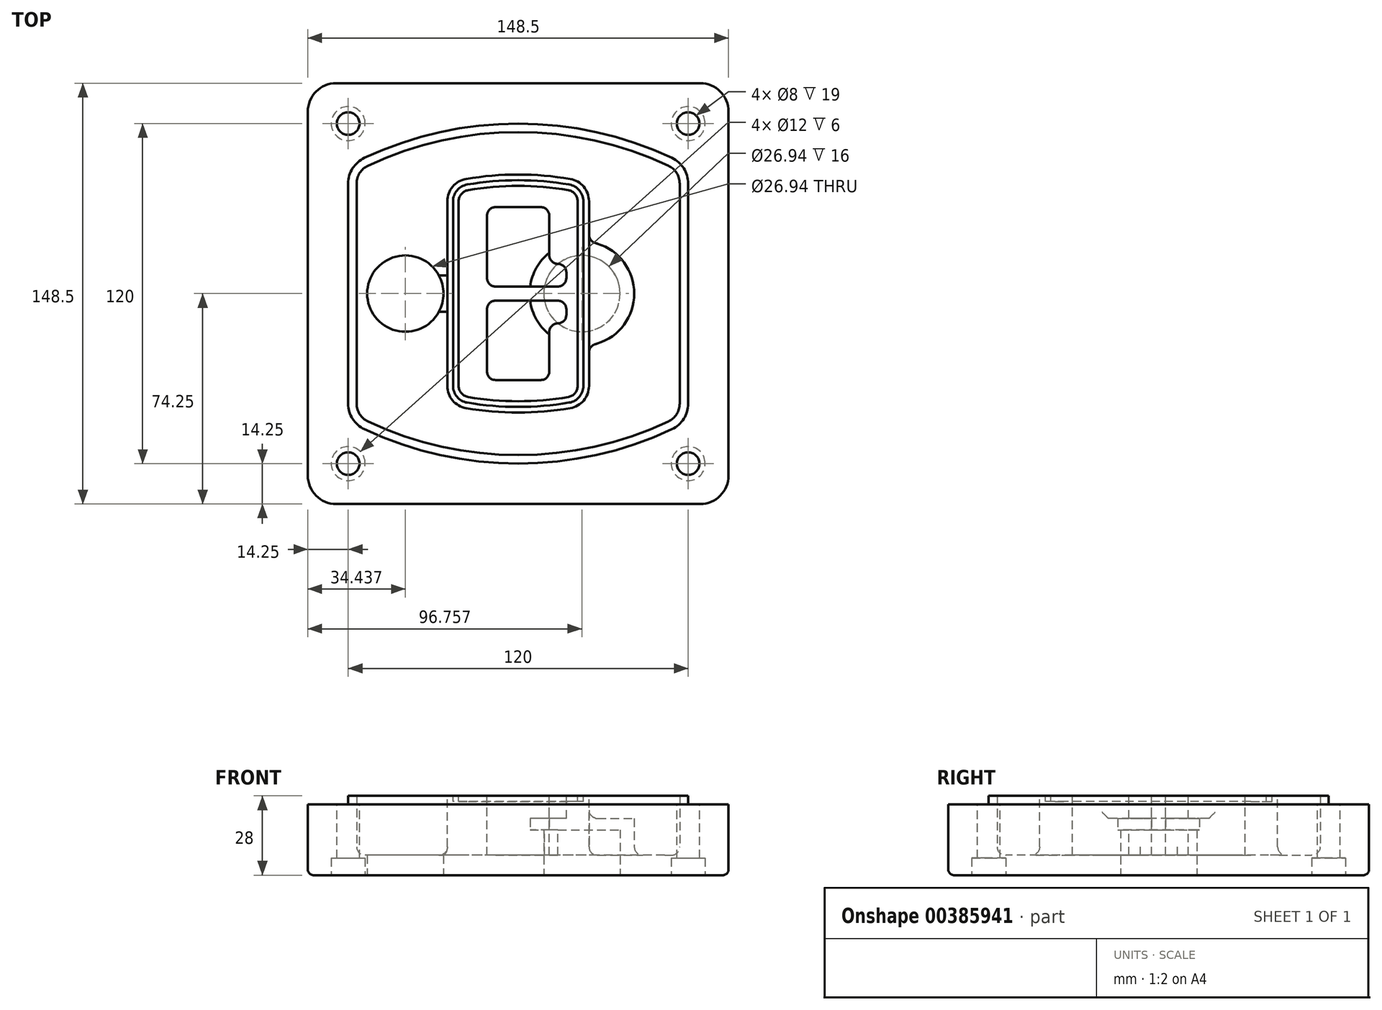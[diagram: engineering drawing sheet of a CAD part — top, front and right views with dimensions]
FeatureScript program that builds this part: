
annotation { "Feature Type Name" : "Feature", "Feature Type Description" : "" }
export const myFeature = defineFeature(function(context is Context, id is Id, definition is map)
    precondition{}
    {
        {
            var Q0;
            Q0=qCreatedBy(makeId("Top.planeOp"),FACE);
            var sketch = newSketch(context, id + "F0", { "sketchPlane" : qUnion([Q0])});
            skPoint(sketch, "E0.rect.middle", {"position": v(0, 0) * mm});
            skLineSegment(sketch, "E1.bottom", {"start": v(-64.25, -74.25) * mm, "end": v(64.25, -74.25) * mm});
            skLineSegment(sketch, "E1.top", {"start": v(-64.25, 74.25) * mm, "end": v(64.25, 74.25) * mm});
            skLineSegment(sketch, "E1.left", {"start": v(-74.25, -64.25) * mm, "end": v(-74.25, 64.25) * mm});
            skLineSegment(sketch, "E1.right", {"start": v(74.25, -64.25) * mm, "end": v(74.25, 64.25) * mm});
            skLineSegment(sketch, "E2", {"start": v(-74.25, 74.25) * mm, "end": v(74.25, -74.25) * mm, "construction": true});
            skLineSegment(sketch, "E3", {"start": v(74.25, 74.25) * mm, "end": v(-74.25, -74.25) * mm, "construction": true});
            skCircle(sketch, "E4", {"center": v(-60, 60) * mm, "radius": 4 * mm});
            skCircle(sketch, "E5", {"center": v(60, 60) * mm, "radius": 4 * mm});
            skCircle(sketch, "E6", {"center": v(60, -60) * mm, "radius": 4 * mm});
            skCircle(sketch, "E7", {"center": v(-60, -60) * mm, "radius": 4 * mm});
            skLineSegment(sketch, "E8", {"start": v(-60, 60) * mm, "end": v(60, 60) * mm, "construction": true});
            skLineSegment(sketch, "E9", {"start": v(60, 60) * mm, "end": v(60, -60) * mm, "construction": true});
            skLineSegment(sketch, "E10", {"start": v(60, -60) * mm, "end": v(-60, -60) * mm, "construction": true});
            skLineSegment(sketch, "E11", {"start": v(-60, -60) * mm, "end": v(-60, 60) * mm, "construction": true});
            skLineSegment(sketch, "E12", {"start": v(-60, 38.83) * mm, "end": v(-60, -38.83) * mm});
            skLineSegment(sketch, "E13", {"start": v(60, 38.83) * mm, "end": v(60, -38.83) * mm});
            skArc(sketch, "E14", {"start": v(54.26, 47.88) * mm, "mid": v(0, 60) * mm, "end": v(-54.26, 47.88) * mm});
            skArc(sketch, "E15", {"start": v(-54.26, -47.88) * mm, "mid": v(0, -60) * mm, "end": v(54.26, -47.88) * mm});
            skLineSegment(sketch, "E16", {"start": v(-60, 0) * mm, "end": v(60, 0) * mm, "construction": true});
            skPoint(sketch, "E17.visualSharp", {"position": v(-60, -45) * mm});
            skArc(sketch, "E17.filletArc", {"start": v(-60, -38.83) * mm, "mid": v(-58.44, -44.2) * mm, "end": v(-54.26, -47.88) * mm});
            skPoint(sketch, "E18.visualSharp", {"position": v(-60, 45) * mm});
            skArc(sketch, "E18.filletArc", {"start": v(-54.26, 47.88) * mm, "mid": v(-58.44, 44.2) * mm, "end": v(-60, 38.83) * mm});
            skPoint(sketch, "E19.visualSharp", {"position": v(60, 45) * mm});
            skArc(sketch, "E19.filletArc", {"start": v(60, 38.83) * mm, "mid": v(58.44, 44.2) * mm, "end": v(54.26, 47.88) * mm});
            skPoint(sketch, "E20.visualSharp", {"position": v(60, -45) * mm});
            skArc(sketch, "E20.filletArc", {"start": v(54.26, -47.88) * mm, "mid": v(58.44, -44.2) * mm, "end": v(60, -38.83) * mm});
            skPoint(sketch, "E21.visualSharp", {"position": v(-74.25, 74.25) * mm});
            skArc(sketch, "E21.filletArc", {"start": v(-64.25, 74.25) * mm, "mid": v(-71.32, 71.32) * mm, "end": v(-74.25, 64.25) * mm});
            skPoint(sketch, "E22.visualSharp", {"position": v(74.25, 74.25) * mm});
            skArc(sketch, "E22.filletArc", {"start": v(74.25, 64.25) * mm, "mid": v(71.32, 71.32) * mm, "end": v(64.25, 74.25) * mm});
            skPoint(sketch, "E23.visualSharp", {"position": v(74.25, -74.25) * mm});
            skArc(sketch, "E23.filletArc", {"start": v(64.25, -74.25) * mm, "mid": v(71.32, -71.32) * mm, "end": v(74.25, -64.25) * mm});
            skPoint(sketch, "E24.visualSharp", {"position": v(-74.25, -74.25) * mm});
            skArc(sketch, "E24.filletArc", {"start": v(-74.25, -64.25) * mm, "mid": v(-71.32, -71.32) * mm, "end": v(-64.25, -74.25) * mm});
            skArc(sketch, "E25.0", {"start": v(57, 38.83) * mm, "mid": v(55.9, 42.58) * mm, "end": v(52.98, 45.17) * mm});
            skLineSegment(sketch, "E25.1", {"start": v(57, 38.83) * mm, "end": v(57, -38.83) * mm});
            skArc(sketch, "E25.2", {"start": v(52.98, -45.17) * mm, "mid": v(55.9, -42.58) * mm, "end": v(57, -38.83) * mm});
            skArc(sketch, "E25.3", {"start": v(-52.98, -45.17) * mm, "mid": v(0, -57) * mm, "end": v(52.98, -45.17) * mm});
            skArc(sketch, "E25.4", {"start": v(-57, -38.83) * mm, "mid": v(-55.9, -42.58) * mm, "end": v(-52.98, -45.17) * mm});
            skArc(sketch, "E25.5", {"start": v(52.98, 45.17) * mm, "mid": v(0, 57) * mm, "end": v(-52.98, 45.17) * mm});
            skLineSegment(sketch, "E25.6", {"start": v(-57, 38.83) * mm, "end": v(-57, -38.83) * mm});
            skArc(sketch, "E25.7", {"start": v(-52.98, 45.17) * mm, "mid": v(-55.9, 42.58) * mm, "end": v(-57, 38.83) * mm});
            skArc(sketch, "E26.0", {"start": v(-55.96, 51.5) * mm, "mid": v(-61.82, 46.33) * mm, "end": v(-64, 38.83) * mm});
            skArc(sketch, "E26.1", {"start": v(55.96, 51.5) * mm, "mid": v(0, 64) * mm, "end": v(-55.96, 51.5) * mm});
            skArc(sketch, "E26.2", {"start": v(64, 38.83) * mm, "mid": v(61.82, 46.33) * mm, "end": v(55.96, 51.5) * mm});
            skLineSegment(sketch, "E26.3", {"start": v(64, 38.83) * mm, "end": v(64, -38.83) * mm});
            skArc(sketch, "E26.4", {"start": v(55.96, -51.5) * mm, "mid": v(61.82, -46.33) * mm, "end": v(64, -38.83) * mm});
            skLineSegment(sketch, "E26.5", {"start": v(-64, 38.83) * mm, "end": v(-64, -38.83) * mm});
            skArc(sketch, "E26.6", {"start": v(-55.96, -51.5) * mm, "mid": v(0, -64) * mm, "end": v(55.96, -51.5) * mm});
            skArc(sketch, "E26.7", {"start": v(-64, -38.83) * mm, "mid": v(-61.82, -46.33) * mm, "end": v(-55.96, -51.5) * mm});
            skCircle(sketch, "E27", {"center": v(0, 95) * mm, "radius": 6 * mm});
            skArc(sketch, "E28", {"start": v(7.76, 95) * mm, "mid": v(-7.24, 110.1) * mm, "end": v(-22.24, 95) * mm});
            skSolve(sketch);
        }
        {
            var Q0;
            Q0=makeQuery(id+"F0.imprint","IMPRINT",FACE,{"disambiguationData":[TD([[makeQuery(id+"F0.imprint","IMPRINT",EDGE,{"derivedFrom":sQuery(id+"F0.wireOp",EDGE,"E1.bottom")}),1.0]])]});
            var Q1;
            Q1=makeQuery(id+"F0.imprint","IMPRINT",FACE,{"disambiguationData":[TD([[makeQuery(id+"F0.imprint","IMPRINT",EDGE,{"derivedFrom":sQuery(id+"F0.wireOp",EDGE,"E12")}),1.0]])]});
            var Q2;
            Q2=makeQuery(id+"F0.imprint","IMPRINT",FACE,{"disambiguationData":[TD([[makeQuery(id+"F0.imprint","IMPRINT",EDGE,{"derivedFrom":sQuery(id+"F0.wireOp",EDGE,"E25.0")}),1.0]])]});
            var Q3;
            Q3=makeQuery(id+"F0.imprint","IMPRINT",FACE,{"disambiguationData":[TD([[makeQuery(id+"F0.imprint","IMPRINT",EDGE,{"derivedFrom":sQuery(id+"F0.wireOp",EDGE,"E12")}),-1.0]])]});
            extrude(context, id + "F1", {"entities" : qUnion([Q0, Q1, Q2, Q3]), "oppositeDirection" : true, "depth" : 25 * mm});
        }
        {
            var Q0;
            Q0=makeQuery(id+"F0.imprint","IMPRINT",FACE,{"disambiguationData":[TD([[makeQuery(id+"F0.imprint","IMPRINT",EDGE,{"derivedFrom":sQuery(id+"F0.wireOp",EDGE,"E12")}),1.0]])]});
            extrude(context, id + "F2", {"entities" : qUnion([Q0]), "operationType" : NewBodyOperationType.ADD, "depth" : 3 * mm});
        }
        {
            var Q0;
            Q0=makeQuery(id+"F0.imprint","IMPRINT",FACE,{"disambiguationData":[TD([[makeQuery(id+"F0.imprint","IMPRINT",EDGE,{"derivedFrom":sQuery(id+"F0.wireOp",EDGE,"E25.0")}),1.0]])]});
            extrude(context, id + "F3", {"entities" : qUnion([Q0]), "operationType" : NewBodyOperationType.REMOVE, "oppositeDirection" : true, "depth" : 18 * mm});
        }
        {
            var Q0;
            Q0=makeQuery(id+"F2.opExtrude","CAP_FACE",FACE,{"disambiguationData":[OSD([sQuery(id+"F0.wireOp",EDGE,"E12"),sQuery(id+"F0.wireOp",EDGE,"E13"),sQuery(id+"F0.wireOp",EDGE,"E14"),sQuery(id+"F0.wireOp",EDGE,"E15"),sQuery(id+"F0.wireOp",EDGE,"E17.filletArc"),sQuery(id+"F0.wireOp",EDGE,"E18.filletArc"),sQuery(id+"F0.wireOp",EDGE,"E19.filletArc"),sQuery(id+"F0.wireOp",EDGE,"E20.filletArc"),sQuery(id+"F0.wireOp",EDGE,"E25.0"),sQuery(id+"F0.wireOp",EDGE,"E25.1"),sQuery(id+"F0.wireOp",EDGE,"E25.2"),sQuery(id+"F0.wireOp",EDGE,"E25.3"),sQuery(id+"F0.wireOp",EDGE,"E25.4"),sQuery(id+"F0.wireOp",EDGE,"E25.5"),sQuery(id+"F0.wireOp",EDGE,"E25.6"),sQuery(id+"F0.wireOp",EDGE,"E25.7")])],"isStart":false});
            var sketch = newSketch(context, id + "F4", { "sketchPlane" : qUnion([Q0])});
            skArc(sketch, "E29.0", {"start": v(-18.34, -40.45) * mm, "mid": v(0, -42) * mm, "end": v(18.34, -40.45) * mm});
            skArc(sketch, "E30.0", {"start": v(18.34, 40.45) * mm, "mid": v(0, 42) * mm, "end": v(-18.34, 40.45) * mm});
            skLineSegment(sketch, "E31", {"start": v(-25, 32.57) * mm, "end": v(-25, -32.57) * mm});
            skLineSegment(sketch, "E32", {"start": v(25, 32.57) * mm, "end": v(25, -32.57) * mm});
            skLineSegment(sketch, "E33", {"start": v(-25, 39.1) * mm, "end": v(25, 39.1) * mm, "construction": true});
            skLineSegment(sketch, "E34", {"start": v(-25, -39.1) * mm, "end": v(25, -39.1) * mm, "construction": true});
            skPoint(sketch, "E35.visualSharp", {"position": v(-25, 39.1) * mm});
            skArc(sketch, "E35.filletArc", {"start": v(-18.34, 40.45) * mm, "mid": v(-23.11, 37.73) * mm, "end": v(-25, 32.57) * mm});
            skPoint(sketch, "E36.visualSharp", {"position": v(25, 39.1) * mm});
            skArc(sketch, "E36.filletArc", {"start": v(25, 32.57) * mm, "mid": v(23.11, 37.73) * mm, "end": v(18.34, 40.45) * mm});
            skPoint(sketch, "E37.visualSharp", {"position": v(25, -39.1) * mm});
            skArc(sketch, "E37.filletArc", {"start": v(18.34, -40.45) * mm, "mid": v(23.11, -37.73) * mm, "end": v(25, -32.57) * mm});
            skPoint(sketch, "E38.visualSharp", {"position": v(-25, -39.1) * mm});
            skArc(sketch, "E38.filletArc", {"start": v(-25, -32.57) * mm, "mid": v(-23.11, -37.73) * mm, "end": v(-18.34, -40.45) * mm});
            skArc(sketch, "E39.0", {"start": v(52.98, 45.17) * mm, "mid": v(0, 57) * mm, "end": v(-52.98, 45.17) * mm});
            skArc(sketch, "E39.1", {"start": v(-52.98, 45.17) * mm, "mid": v(-55.9, 42.58) * mm, "end": v(-57, 38.83) * mm});
            skLineSegment(sketch, "E39.2", {"start": v(-57, 38.83) * mm, "end": v(-57, -38.83) * mm});
            skArc(sketch, "E39.3", {"start": v(-57, -38.83) * mm, "mid": v(-55.9, -42.58) * mm, "end": v(-52.98, -45.17) * mm});
            skArc(sketch, "E39.4", {"start": v(-52.98, -45.17) * mm, "mid": v(0, -57) * mm, "end": v(52.98, -45.17) * mm});
            skArc(sketch, "E39.5", {"start": v(52.98, -45.17) * mm, "mid": v(55.9, -42.58) * mm, "end": v(57, -38.83) * mm});
            skLineSegment(sketch, "E39.6", {"start": v(57, 38.83) * mm, "end": v(57, -38.83) * mm});
            skArc(sketch, "E39.7", {"start": v(57, 38.83) * mm, "mid": v(55.9, 42.58) * mm, "end": v(52.98, 45.17) * mm});
            skLineSegment(sketch, "E40.0", {"start": v(23, 32.57) * mm, "end": v(23, -32.57) * mm});
            skArc(sketch, "E40.1", {"start": v(18, -38.48) * mm, "mid": v(21.58, -36.44) * mm, "end": v(23, -32.57) * mm});
            skArc(sketch, "E40.2", {"start": v(-18, -38.48) * mm, "mid": v(0, -40) * mm, "end": v(18, -38.48) * mm});
            skArc(sketch, "E40.3", {"start": v(-23, -32.57) * mm, "mid": v(-21.58, -36.44) * mm, "end": v(-18, -38.48) * mm});
            skLineSegment(sketch, "E40.4", {"start": v(-23, 32.57) * mm, "end": v(-23, -32.57) * mm});
            skArc(sketch, "E40.5", {"start": v(23, 32.57) * mm, "mid": v(21.58, 36.44) * mm, "end": v(18, 38.48) * mm});
            skArc(sketch, "E40.6", {"start": v(-18, 38.48) * mm, "mid": v(-21.58, 36.44) * mm, "end": v(-23, 32.57) * mm});
            skArc(sketch, "E40.7", {"start": v(18, 38.48) * mm, "mid": v(0, 40) * mm, "end": v(-18, 38.48) * mm});
            skArc(sketch, "E41.0", {"start": v(21, 32.57) * mm, "mid": v(20.06, 35.15) * mm, "end": v(17.67, 36.5) * mm});
            skLineSegment(sketch, "E41.1", {"start": v(21, 32.57) * mm, "end": v(21, -32.57) * mm});
            skArc(sketch, "E41.2", {"start": v(17.67, -36.5) * mm, "mid": v(20.06, -35.15) * mm, "end": v(21, -32.57) * mm});
            skArc(sketch, "E41.3", {"start": v(-17.67, -36.5) * mm, "mid": v(0, -38) * mm, "end": v(17.67, -36.5) * mm});
            skArc(sketch, "E41.4", {"start": v(-21, -32.57) * mm, "mid": v(-20.06, -35.15) * mm, "end": v(-17.67, -36.5) * mm});
            skArc(sketch, "E41.5", {"start": v(17.67, 36.5) * mm, "mid": v(0, 38) * mm, "end": v(-17.67, 36.5) * mm});
            skLineSegment(sketch, "E41.6", {"start": v(-21, 32.57) * mm, "end": v(-21, -32.57) * mm});
            skArc(sketch, "E41.7", {"start": v(-17.67, 36.5) * mm, "mid": v(-20.06, 35.15) * mm, "end": v(-21, 32.57) * mm});
            skLineSegment(sketch, "E42", {"start": v(-25, 0) * mm, "end": v(25, 0) * mm, "construction": true});
            skLineSegment(sketch, "E43", {"start": v(-11, 5.5) * mm, "end": v(-11, 27.5) * mm});
            skLineSegment(sketch, "E44", {"start": v(-8, 30.5) * mm, "end": v(8, 30.5) * mm});
            skLineSegment(sketch, "E45", {"start": v(11, 27.5) * mm, "end": v(11, 13.5) * mm});
            skLineSegment(sketch, "E46", {"start": v(14, 10.5) * mm, "end": v(14, 10.5) * mm});
            skLineSegment(sketch, "E47", {"start": v(17, 7.5) * mm, "end": v(17, 5.5) * mm});
            skLineSegment(sketch, "E48", {"start": v(14, 2.5) * mm, "end": v(-8, 2.5) * mm});
            skPoint(sketch, "E49.visualSharp", {"position": v(-11, 30.5) * mm});
            skArc(sketch, "E49.filletArc", {"start": v(-8, 30.5) * mm, "mid": v(-10.12, 29.62) * mm, "end": v(-11, 27.5) * mm});
            skPoint(sketch, "E50.visualSharp", {"position": v(11, 30.5) * mm});
            skArc(sketch, "E50.filletArc", {"start": v(11, 27.5) * mm, "mid": v(10.12, 29.62) * mm, "end": v(8, 30.5) * mm});
            skPoint(sketch, "E51.visualSharp", {"position": v(11, 10.5) * mm});
            skArc(sketch, "E51.filletArc", {"start": v(11, 13.5) * mm, "mid": v(11.88, 11.38) * mm, "end": v(14, 10.5) * mm});
            skPoint(sketch, "E52.visualSharp", {"position": v(17, 10.5) * mm});
            skArc(sketch, "E52.filletArc", {"start": v(17, 7.5) * mm, "mid": v(16.12, 9.62) * mm, "end": v(14, 10.5) * mm});
            skPoint(sketch, "E53.visualSharp", {"position": v(17, 2.5) * mm});
            skArc(sketch, "E53.filletArc", {"start": v(14, 2.5) * mm, "mid": v(16.12, 3.38) * mm, "end": v(17, 5.5) * mm});
            skPoint(sketch, "E54.visualSharp", {"position": v(-11, 2.5) * mm});
            skArc(sketch, "E54.filletArc", {"start": v(-11, 5.5) * mm, "mid": v(-10.12, 3.38) * mm, "end": v(-8, 2.5) * mm});
            skLineSegment(sketch, "E55.0.MirrorCS", {"start": v(14, -2.5) * mm, "end": v(-8, -2.5) * mm});
            skArc(sketch, "E56.0.MirrorCS", {"start": v(-11, -5.5) * mm, "mid": v(-10.12, -3.38) * mm, "end": v(-8, -2.5) * mm});
            skLineSegment(sketch, "E57.0.MirrorCS", {"start": v(-11, -5.5) * mm, "end": v(-11, -27.5) * mm});
            skArc(sketch, "E58.0.MirrorCS", {"start": v(-8, -30.5) * mm, "mid": v(-10.12, -29.62) * mm, "end": v(-11, -27.5) * mm});
            skLineSegment(sketch, "E59.0.MirrorCS", {"start": v(-8, -30.5) * mm, "end": v(8, -30.5) * mm});
            skArc(sketch, "E60.0.MirrorCS", {"start": v(11, -27.5) * mm, "mid": v(10.12, -29.62) * mm, "end": v(8, -30.5) * mm});
            skLineSegment(sketch, "E61.0.MirrorCS", {"start": v(11, -27.5) * mm, "end": v(11, -13.5) * mm});
            skArc(sketch, "E62.0.MirrorCS", {"start": v(11, -13.5) * mm, "mid": v(11.88, -11.38) * mm, "end": v(14, -10.5) * mm});
            skArc(sketch, "E63.0.MirrorCS", {"start": v(17, -7.5) * mm, "mid": v(16.12, -9.62) * mm, "end": v(14, -10.5) * mm});
            skLineSegment(sketch, "E64.0.MirrorCS", {"start": v(17, -7.5) * mm, "end": v(17, -5.5) * mm});
            skArc(sketch, "E65.0.MirrorCS", {"start": v(14, -2.5) * mm, "mid": v(16.12, -3.38) * mm, "end": v(17, -5.5) * mm});
            skSolve(sketch);
        }
        {
            var Q0;
            Q0=makeQuery(id+"F4.imprint","IMPRINT",FACE,{"disambiguationData":[TD([[makeQuery(id+"F4.imprint","IMPRINT",EDGE,{"derivedFrom":sQuery(id+"F4.wireOp",EDGE,"E29.0")}),1.0]])]});
            var Q1;
            Q1=makeQuery(id+"F4.imprint","IMPRINT",FACE,{"disambiguationData":[TD([[makeQuery(id+"F4.imprint","IMPRINT",EDGE,{"derivedFrom":sQuery(id+"F4.wireOp",EDGE,"E40.0")}),-1.0]])]});
            var Q2;
            Q2=makeQuery(id+"F4.imprint","IMPRINT",FACE,{"disambiguationData":[TD([[makeQuery(id+"F4.imprint","IMPRINT",EDGE,{"derivedFrom":sQuery(id+"F4.wireOp",EDGE,"E41.0")}),1.0]])]});
            extrude(context, id + "F5", {"entities" : qUnion([Q0, Q1, Q2]), "operationType" : NewBodyOperationType.ADD, "endBound" : BoundingType.UP_TO_NEXT, "oppositeDirection" : true, "depth" : 25 * mm});
        }
        {
            var Q0;
            Q0=makeQuery(id+"F4.imprint","IMPRINT",FACE,{"disambiguationData":[TD([[makeQuery(id+"F4.imprint","IMPRINT",EDGE,{"derivedFrom":sQuery(id+"F4.wireOp",EDGE,"E40.0")}),-1.0]])]});
            extrude(context, id + "F6", {"entities" : qUnion([Q0]), "operationType" : NewBodyOperationType.REMOVE, "oppositeDirection" : true, "depth" : 2 * mm});
        }
        {
            var Q0;
            Q0=makeQuery(id+"F1.opExtrude","CAP_FACE",FACE,{"disambiguationData":[OSD([sQuery(id+"F0.wireOp",EDGE,"E1.bottom"),sQuery(id+"F0.wireOp",EDGE,"E1.top"),sQuery(id+"F0.wireOp",EDGE,"E1.left"),sQuery(id+"F0.wireOp",EDGE,"E1.right"),sQuery(id+"F0.wireOp",EDGE,"E4"),sQuery(id+"F0.wireOp",EDGE,"E5"),sQuery(id+"F0.wireOp",EDGE,"E6"),sQuery(id+"F0.wireOp",EDGE,"E7"),sQuery(id+"F0.wireOp",EDGE,"E21.filletArc"),sQuery(id+"F0.wireOp",EDGE,"E22.filletArc"),sQuery(id+"F0.wireOp",EDGE,"E23.filletArc"),sQuery(id+"F0.wireOp",EDGE,"E24.filletArc")])],"isStart":false});
            var sketch = newSketch(context, id + "F7", { "sketchPlane" : qUnion([Q0])});
            skCircle(sketch, "E66", {"center": v(22.5, 0) * mm, "radius": 13.47 * mm});
            skCircle(sketch, "E67", {"center": v(-39.81, 0) * mm, "radius": 13.47 * mm});
            skLineSegment(sketch, "E68", {"start": v(74.25, 0) * mm, "end": v(-74.25, 0) * mm});
            skCircle(sketch, "E69", {"center": v(22.5, 0) * mm, "radius": 18.47 * mm});
            skCircle(sketch, "E70", {"center": v(60, -60) * mm, "radius": 6 * mm});
            skCircle(sketch, "E71", {"center": v(-60, -60) * mm, "radius": 6 * mm});
            skCircle(sketch, "E72", {"center": v(-60, 60) * mm, "radius": 6 * mm});
            skCircle(sketch, "E73", {"center": v(60, 60) * mm, "radius": 6 * mm});
            skSolve(sketch);
        }
        {
            var Q0;
            {var subQ1=sQuery(id+"F7.wireOp",EDGE,"E68");var subQ4=sQuery(id+"F7.wireOp",EDGE,"E66");var subQ6=makeQuery(id+"F7.imprint","INTERSECT",VERTEX,{"disambiguationData":[OD(0.0)],"derivedFrom":[subQ4,subQ1]});Q0=makeQuery(id+"F7.imprint","IMPRINT",FACE,{"disambiguationData":[TD([[makeQuery(id+"F7.imprint","IMPRINT",EDGE,{"disambiguationData":[TD([[subQ6,-1.0]])],"derivedFrom":subQ4}),-1.0]])]});}
            var Q1;
            {var subQ0=sQuery(id+"F7.wireOp",EDGE,"E68");var subQ1=sQuery(id+"F7.wireOp",EDGE,"E66");var subQ3=makeQuery(id+"F7.imprint","INTERSECT",VERTEX,{"disambiguationData":[OD(0.0)],"derivedFrom":[subQ1,subQ0]});Q1=makeQuery(id+"F7.imprint","IMPRINT",FACE,{"disambiguationData":[TD([[makeQuery(id+"F7.imprint","IMPRINT",EDGE,{"disambiguationData":[TD([[subQ3,-1.0]])],"derivedFrom":subQ1}),1.0]])]});}
            var Q2;
            {var subQ0=sQuery(id+"F7.wireOp",EDGE,"E68");var subQ1=sQuery(id+"F7.wireOp",EDGE,"E66");var subQ3=makeQuery(id+"F7.imprint","INTERSECT",VERTEX,{"disambiguationData":[OD(0.0)],"derivedFrom":[subQ1,subQ0]});Q2=makeQuery(id+"F7.imprint","IMPRINT",FACE,{"disambiguationData":[TD([[makeQuery(id+"F7.imprint","IMPRINT",EDGE,{"disambiguationData":[TD([[subQ3,1.0]])],"derivedFrom":subQ1}),1.0]])]});}
            var Q3;
            {var subQ1=sQuery(id+"F7.wireOp",EDGE,"E68");var subQ4=sQuery(id+"F7.wireOp",EDGE,"E66");var subQ6=makeQuery(id+"F7.imprint","INTERSECT",VERTEX,{"disambiguationData":[OD(0.0)],"derivedFrom":[subQ4,subQ1]});Q3=makeQuery(id+"F7.imprint","IMPRINT",FACE,{"disambiguationData":[TD([[makeQuery(id+"F7.imprint","IMPRINT",EDGE,{"disambiguationData":[TD([[subQ6,1.0]])],"derivedFrom":subQ4}),-1.0]])]});}
            extrude(context, id + "F8", {"entities" : qUnion([Q0, Q1, Q2, Q3]), "operationType" : NewBodyOperationType.ADD, "oppositeDirection" : true, "depth" : 20 * mm});
        }
        {
            var Q0;
            {var subQ0=sQuery(id+"F7.wireOp",EDGE,"E68");var subQ1=sQuery(id+"F7.wireOp",EDGE,"E66");var subQ3=makeQuery(id+"F7.imprint","INTERSECT",VERTEX,{"disambiguationData":[OD(0.0)],"derivedFrom":[subQ1,subQ0]});Q0=makeQuery(id+"F7.imprint","IMPRINT",FACE,{"disambiguationData":[TD([[makeQuery(id+"F7.imprint","IMPRINT",EDGE,{"disambiguationData":[TD([[subQ3,-1.0]])],"derivedFrom":subQ1}),1.0]])]});}
            var Q1;
            {var subQ0=sQuery(id+"F7.wireOp",EDGE,"E68");var subQ1=sQuery(id+"F7.wireOp",EDGE,"E66");var subQ3=makeQuery(id+"F7.imprint","INTERSECT",VERTEX,{"disambiguationData":[OD(0.0)],"derivedFrom":[subQ1,subQ0]});Q1=makeQuery(id+"F7.imprint","IMPRINT",FACE,{"disambiguationData":[TD([[makeQuery(id+"F7.imprint","IMPRINT",EDGE,{"disambiguationData":[TD([[subQ3,1.0]])],"derivedFrom":subQ1}),1.0]])]});}
            extrude(context, id + "F9", {"entities" : qUnion([Q0, Q1]), "operationType" : NewBodyOperationType.REMOVE, "oppositeDirection" : true, "depth" : 16 * mm});
        }
        {
            var Q0;
            {var subQ0=sQuery(id+"F7.wireOp",EDGE,"E68");var subQ1=sQuery(id+"F7.wireOp",EDGE,"E67");var subQ3=makeQuery(id+"F7.imprint","INTERSECT",VERTEX,{"disambiguationData":[OD(0.0)],"derivedFrom":[subQ1,subQ0]});Q0=makeQuery(id+"F7.imprint","IMPRINT",FACE,{"disambiguationData":[TD([[makeQuery(id+"F7.imprint","IMPRINT",EDGE,{"disambiguationData":[TD([[subQ3,-1.0]])],"derivedFrom":subQ1}),1.0]])]});}
            var Q1;
            {var subQ0=sQuery(id+"F7.wireOp",EDGE,"E68");var subQ1=sQuery(id+"F7.wireOp",EDGE,"E67");var subQ3=makeQuery(id+"F7.imprint","INTERSECT",VERTEX,{"disambiguationData":[OD(0.0)],"derivedFrom":[subQ1,subQ0]});Q1=makeQuery(id+"F7.imprint","IMPRINT",FACE,{"disambiguationData":[TD([[makeQuery(id+"F7.imprint","IMPRINT",EDGE,{"disambiguationData":[TD([[subQ3,1.0]])],"derivedFrom":subQ1}),1.0]])]});}
            extrude(context, id + "F10", {"entities" : qUnion([Q0, Q1]), "operationType" : NewBodyOperationType.REMOVE, "oppositeDirection" : true, "depth" : 25 * mm});
        }
        {
            var Q0;
            Q0=makeQuery(id+"F7.imprint","IMPRINT",FACE,{"disambiguationData":[TD([[makeQuery(id+"F7.imprint","IMPRINT",EDGE,{"derivedFrom":sQuery(id+"F7.wireOp",EDGE,"E70")}),1.0]])]});
            var Q1;
            Q1=makeQuery(id+"F7.imprint","IMPRINT",FACE,{"disambiguationData":[TD([[makeQuery(id+"F7.imprint","IMPRINT",EDGE,{"derivedFrom":makeQuery(id+"F1.opExtrude","CAP_EDGE",EDGE,{"disambiguationData":[OSD([sQuery(id+"F0.wireOp",EDGE,"E5")])],"isStart":false})}),-1.0]])]});
            var Q2;
            Q2=makeQuery(id+"F7.imprint","IMPRINT",FACE,{"disambiguationData":[TD([[makeQuery(id+"F7.imprint","IMPRINT",EDGE,{"derivedFrom":sQuery(id+"F7.wireOp",EDGE,"E71")}),1.0]])]});
            var Q3;
            Q3=makeQuery(id+"F7.imprint","IMPRINT",FACE,{"disambiguationData":[TD([[makeQuery(id+"F7.imprint","IMPRINT",EDGE,{"derivedFrom":makeQuery(id+"F1.opExtrude","CAP_EDGE",EDGE,{"disambiguationData":[OSD([sQuery(id+"F0.wireOp",EDGE,"E4")])],"isStart":false})}),-1.0]])]});
            var Q4;
            Q4=makeQuery(id+"F7.imprint","IMPRINT",FACE,{"disambiguationData":[TD([[makeQuery(id+"F7.imprint","IMPRINT",EDGE,{"derivedFrom":sQuery(id+"F7.wireOp",EDGE,"E72")}),1.0]])]});
            var Q5;
            Q5=makeQuery(id+"F7.imprint","IMPRINT",FACE,{"disambiguationData":[TD([[makeQuery(id+"F7.imprint","IMPRINT",EDGE,{"derivedFrom":makeQuery(id+"F1.opExtrude","CAP_EDGE",EDGE,{"disambiguationData":[OSD([sQuery(id+"F0.wireOp",EDGE,"E7")])],"isStart":false})}),-1.0]])]});
            var Q6;
            Q6=makeQuery(id+"F7.imprint","IMPRINT",FACE,{"disambiguationData":[TD([[makeQuery(id+"F7.imprint","IMPRINT",EDGE,{"derivedFrom":sQuery(id+"F7.wireOp",EDGE,"E73")}),1.0]])]});
            var Q7;
            Q7=makeQuery(id+"F7.imprint","IMPRINT",FACE,{"disambiguationData":[TD([[makeQuery(id+"F7.imprint","IMPRINT",EDGE,{"derivedFrom":makeQuery(id+"F1.opExtrude","CAP_EDGE",EDGE,{"disambiguationData":[OSD([sQuery(id+"F0.wireOp",EDGE,"E6")])],"isStart":false})}),-1.0]])]});
            extrude(context, id + "F11", {"entities" : qUnion([Q0, Q1, Q2, Q3, Q4, Q5, Q6, Q7]), "operationType" : NewBodyOperationType.REMOVE, "oppositeDirection" : true, "depth" : 6 * mm});
        }
        {
            var Q0;
            Q0=makeQuery(id+"F9.boolean.opBoolean","COPY",FACE,{"derivedFrom":makeQuery(id+"F9.opExtrude","CAP_FACE",FACE,{"disambiguationData":[OSD([sQuery(id+"F7.wireOp",EDGE,"E66")])],"isStart":false})});
            var sketch = newSketch(context, id + "F12", { "sketchPlane" : qUnion([Q0])});
            skArc(sketch, "E74.0", {"start": v(11, 14.45) * mm, "mid": v(6.45, 9.13) * mm, "end": v(4.2, 2.5) * mm});
            skArc(sketch, "E74.1", {"start": v(4.2, -2.5) * mm, "mid": v(6.45, -9.13) * mm, "end": v(11, -14.45) * mm});
            skLineSegment(sketch, "E75", {"start": v(4.2, -2.5) * mm, "end": v(14, -2.5) * mm});
            skLineSegment(sketch, "E76.0", {"start": v(14, 2.5) * mm, "end": v(4.2, 2.5) * mm});
            skArc(sketch, "E76.1", {"start": v(14, 2.5) * mm, "mid": v(16.12, 3.38) * mm, "end": v(17, 5.5) * mm});
            skLineSegment(sketch, "E76.2", {"start": v(17, 7.5) * mm, "end": v(17, 5.5) * mm});
            skArc(sketch, "E76.3", {"start": v(17, 7.5) * mm, "mid": v(16.12, 9.62) * mm, "end": v(14, 10.5) * mm});
            skArc(sketch, "E76.4", {"start": v(11, 13.5) * mm, "mid": v(11.88, 11.38) * mm, "end": v(14, 10.5) * mm});
            skLineSegment(sketch, "E76.5", {"start": v(11, 14.45) * mm, "end": v(11, 13.5) * mm});
            skLineSegment(sketch, "E76.7", {"start": v(14, -2.5) * mm, "end": v(4.2, -2.5) * mm});
            skArc(sketch, "E76.8", {"start": v(14, -2.5) * mm, "mid": v(16.12, -3.38) * mm, "end": v(17, -5.5) * mm});
            skLineSegment(sketch, "E76.9", {"start": v(17, -7.5) * mm, "end": v(17, -5.5) * mm});
            skArc(sketch, "E76.10", {"start": v(17, -7.5) * mm, "mid": v(16.12, -9.62) * mm, "end": v(14, -10.5) * mm});
            skArc(sketch, "E76.11", {"start": v(11, -13.5) * mm, "mid": v(11.88, -11.38) * mm, "end": v(14, -10.5) * mm});
            skLineSegment(sketch, "E76.12", {"start": v(11, -14.45) * mm, "end": v(11, -13.5) * mm});
            skPoint(sketch, "E77.orphan", {"position": v(11, -27.5) * mm});
            skPoint(sketch, "E78.orphan", {"position": v(-8, -2.5) * mm});
            skPoint(sketch, "E79.orphan", {"position": v(-8, 2.5) * mm});
            skPoint(sketch, "E80.orphan", {"position": v(11, 27.5) * mm});
            skSolve(sketch);
        }
        {
            var Q0;
            {var subQ7=sQuery(id+"F12.wireOp",EDGE,"E74.0");var subQ14=sQuery(id+"F12.wireOp",EDGE,"E74.1");var subQ16=sQuery(id+"F12.wireOp",EDGE,"E76.1");var subQ18=sQuery(id+"F12.wireOp",EDGE,"E76.8");Q0=qUnion([makeQuery(id+"F12.imprint","IMPRINT",FACE,{"disambiguationData":[TD([[makeQuery(id+"F12.imprint","IMPRINT",EDGE,{"derivedFrom":subQ7}),1.0]])]}),makeQuery(id+"F12.imprint","IMPRINT",FACE,{"disambiguationData":[TD([[makeQuery(id+"F12.imprint","IMPRINT",EDGE,{"derivedFrom":subQ14}),1.0]])]}),makeQuery(id+"F12.imprint","IMPRINT",FACE,{"disambiguationData":[TD([[makeQuery(id+"F12.imprint","IMPRINT",EDGE,{"derivedFrom":subQ16}),1.0]])]}),makeQuery(id+"F12.imprint","IMPRINT",FACE,{"disambiguationData":[TD([[makeQuery(id+"F12.imprint","IMPRINT",EDGE,{"derivedFrom":subQ18}),-1.0]])]})]);}
            var Q1;
            Q1=makeQuery(id+"F5.boolean.opBoolean","SPLIT",FACE,{"disambiguationData":[TD([makeQuery(id+"F5.opExtrude","SWEPT_FACE",FACE,{"disambiguationData":[OSD([sQuery(id+"F4.wireOp",EDGE,"E43")])]})])],"derivedFrom":makeQuery(id+"F3.boolean.opBoolean","COPY",FACE,{"derivedFrom":makeQuery(id+"F3.opExtrude","CAP_FACE",FACE,{"disambiguationData":[OSD([sQuery(id+"F0.wireOp",EDGE,"E25.0"),sQuery(id+"F0.wireOp",EDGE,"E25.1"),sQuery(id+"F0.wireOp",EDGE,"E25.2"),sQuery(id+"F0.wireOp",EDGE,"E25.3"),sQuery(id+"F0.wireOp",EDGE,"E25.4"),sQuery(id+"F0.wireOp",EDGE,"E25.5"),sQuery(id+"F0.wireOp",EDGE,"E25.6"),sQuery(id+"F0.wireOp",EDGE,"E25.7")])],"isStart":false})})});
            extrude(context, id + "F13", {"entities" : qUnion([Q0]), "operationType" : NewBodyOperationType.REMOVE, "endBound" : BoundingType.UP_TO_SURFACE, "endBoundEntityFace" : qUnion([Q1]), "depth" : 25 * mm});
        }
        {
            var Q0;
            Q0=makeQuery(id+"F3.boolean.opBoolean","COPY",EDGE,{"derivedFrom":makeQuery(id+"F3.opExtrude","CAP_EDGE",EDGE,{"disambiguationData":[OSD([sQuery(id+"F0.wireOp",EDGE,"E25.6")])],"isStart":false})});
            var Q1;
            Q1=makeQuery(id+"F8.boolean.opBoolean","INTERSECT",EDGE,{"derivedFrom":[makeQuery(id+"F5.opExtrude","SWEPT_FACE",FACE,{"disambiguationData":[OSD([sQuery(id+"F4.wireOp",EDGE,"E32")])]}),makeQuery(id+"F8.opExtrude","CAP_FACE",FACE,{"disambiguationData":[OSD([sQuery(id+"F7.wireOp",EDGE,"E69")])],"isStart":false})]});
            var Q2;
            Q2=makeQuery(id+"F8.boolean.opBoolean","INTERSECT",EDGE,{"disambiguationData":[OD(1.0)],"derivedFrom":[makeQuery(id+"F5.opExtrude","SWEPT_FACE",FACE,{"disambiguationData":[OSD([sQuery(id+"F4.wireOp",EDGE,"E32")])]}),makeQuery(id+"F8.opExtrude","SWEPT_FACE",FACE,{"disambiguationData":[OSD([sQuery(id+"F7.wireOp",EDGE,"E69")])]})]});
            var Q3;
            {var subQ0=sQuery(id+"F4.wireOp",EDGE,"E32");Q3=makeQuery(id+"F8.boolean.opBoolean","SPLIT",EDGE,{"disambiguationData":[TD([makeQuery(id+"F5.opExtrude","SWEPT_FACE",FACE,{"disambiguationData":[OSD([sQuery(id+"F4.wireOp",EDGE,"E37.filletArc")])]})])],"derivedFrom":makeQuery(id+"F5.opExtrude","CAP_EDGE",EDGE,{"disambiguationData":[OSD([subQ0])],"isStart":false})});}
            var Q4;
            {var subQ0=sQuery(id+"F0.wireOp",EDGE,"E25.7");var subQ1=sQuery(id+"F0.wireOp",EDGE,"E25.1");var subQ2=sQuery(id+"F0.wireOp",EDGE,"E25.6");var subQ3=sQuery(id+"F0.wireOp",EDGE,"E25.5");var subQ4=sQuery(id+"F0.wireOp",EDGE,"E25.4");var subQ5=sQuery(id+"F0.wireOp",EDGE,"E25.0");var subQ6=sQuery(id+"F0.wireOp",EDGE,"E25.2");var subQ7=sQuery(id+"F0.wireOp",EDGE,"E25.3");Q4=makeQuery(id+"F8.boolean.opBoolean","INTERSECT",EDGE,{"derivedFrom":[makeQuery(id+"F5.boolean.opBoolean","SPLIT",FACE,{"disambiguationData":[TD([makeQuery(id+"F2.opExtrude","SWEPT_FACE",FACE,{"disambiguationData":[OSD([subQ5])]})])],"derivedFrom":makeQuery(id+"F3.boolean.opBoolean","COPY",FACE,{"derivedFrom":makeQuery(id+"F3.opExtrude","CAP_FACE",FACE,{"disambiguationData":[OSD([subQ5,subQ1,subQ6,subQ7,subQ4,subQ3,subQ2,subQ0])],"isStart":false})})}),makeQuery(id+"F8.opExtrude","SWEPT_FACE",FACE,{"disambiguationData":[OSD([sQuery(id+"F7.wireOp",EDGE,"E69")])]})]});}
            var Q5;
            Q5=makeQuery(id+"F8.boolean.opBoolean","INTERSECT",EDGE,{"disambiguationData":[OD(0.0)],"derivedFrom":[makeQuery(id+"F5.opExtrude","SWEPT_FACE",FACE,{"disambiguationData":[OSD([sQuery(id+"F4.wireOp",EDGE,"E32")])]}),makeQuery(id+"F8.opExtrude","SWEPT_FACE",FACE,{"disambiguationData":[OSD([sQuery(id+"F7.wireOp",EDGE,"E69")])]})]});
            fillet(context, id + "F14", {"entities" : qUnion([Q0, Q1, Q2, Q3, Q4, Q5]), "radius" : 3 * mm, "tangentPropagation" : true, "allowEdgeOverflow" : false});
        }
        {
            var Q0;
            Q0=makeQuery(id+"F1.opExtrude","CAP_EDGE",EDGE,{"disambiguationData":[OSD([sQuery(id+"F0.wireOp",EDGE,"E1.bottom")])],"isStart":false});
            fillet(context, id + "F15", {"entities" : qUnion([Q0]), "radius" : 2 * mm, "tangentPropagation" : true, "allowEdgeOverflow" : false});
        }
    });
